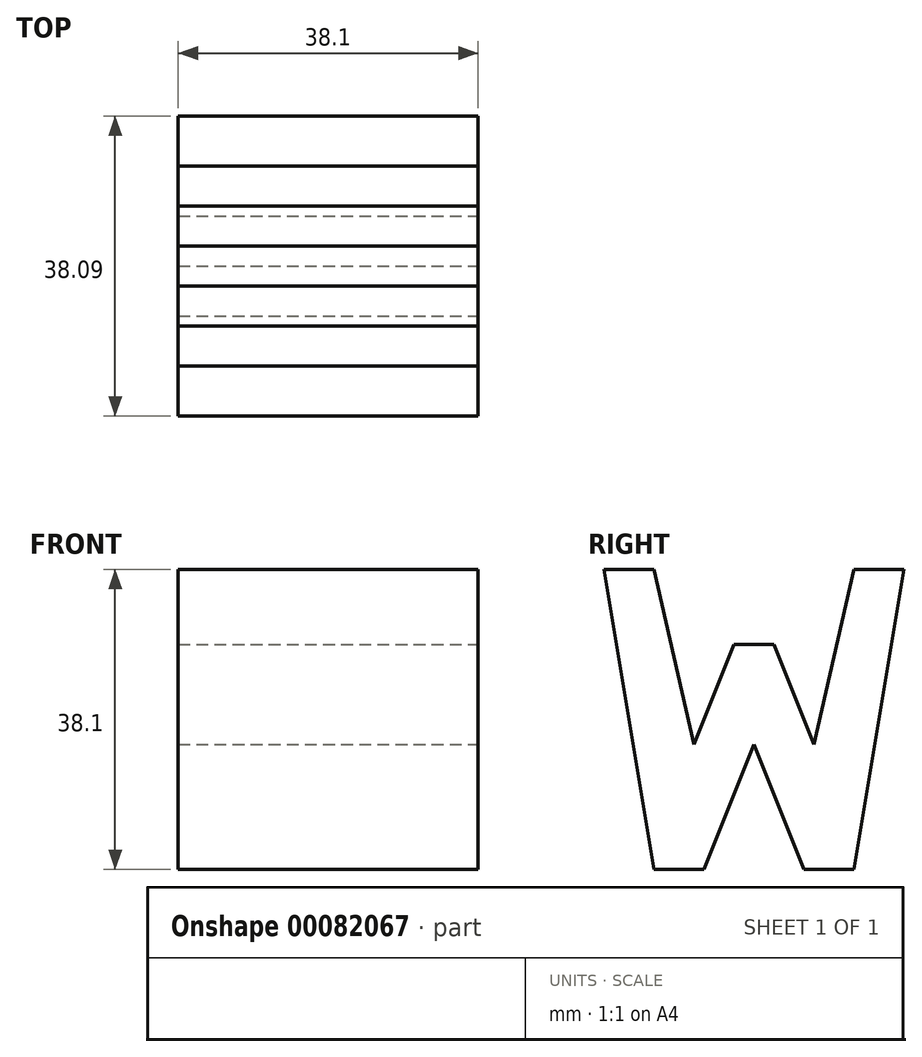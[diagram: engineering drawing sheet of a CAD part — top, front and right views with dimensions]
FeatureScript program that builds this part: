
annotation { "Feature Type Name" : "Feature", "Feature Type Description" : "" }
export const myFeature = defineFeature(function(context is Context, id is Id, definition is map)
    precondition{}
    {
        {
            var Q0;
            Q0=qCreatedBy(makeId("Front.planeOp"),FACE);
            var sketch = newSketch(context, id + "F0", { "sketchPlane" : qUnion([Q0])});
            skLineSegment(sketch, "E0", {"start": v(0, 0) * mm, "end": v(38.1, 0) * mm});
            skLineSegment(sketch, "E1", {"start": v(38.1, 0) * mm, "end": v(38.1, 38.1) * mm});
            skLineSegment(sketch, "E2", {"start": v(38.1, 38.1) * mm, "end": v(0, 38.1) * mm});
            skLineSegment(sketch, "E3", {"start": v(0, 38.1) * mm, "end": v(0, 0) * mm});
            skSolve(sketch);
        }
        {
            var Q0;
            Q0 = qSketchRegion(id + "F0", true);
            extrude(context, id + "F1", {"entities" : qUnion([Q0]), "depth" : 38.1 * mm});
        }
        {
            var Q0;
            Q0=qCreatedBy(makeId("Right.planeOp"),FACE);
            cPlane(context, id + "F2", {"entities" : qUnion([Q0]), "cplaneType" : CPlaneType.OFFSET, "offset" : 38.1 * mm, "width" : 152.4 * mm, "height" : 152.4 * mm});
        }
        {
            var Q0;
            Q0=qCreatedBy(id+"F2.planeOp",FACE);
            var sketch = newSketch(context, id + "F3", { "sketchPlane" : qUnion([Q0])});
            skLineSegment(sketch, "E4", {"start": v(-38.1, 38.14) * mm, "end": v(-31.75, 0) * mm});
            skLineSegment(sketch, "E5", {"start": v(-31.75, 0) * mm, "end": v(-25.4, 0) * mm});
            skLineSegment(sketch, "E6", {"start": v(-25.4, 0) * mm, "end": v(-19.05, 15.87) * mm});
            skLineSegment(sketch, "E7", {"start": v(-19.05, 15.88) * mm, "end": v(-12.7, 0) * mm});
            skLineSegment(sketch, "E8", {"start": v(-12.7, 0) * mm, "end": v(-6.35, 0) * mm});
            skLineSegment(sketch, "E9", {"start": v(-6.35, 0) * mm, "end": v(0, 38.1) * mm});
            skLineSegment(sketch, "E10", {"start": v(0, 38.1) * mm, "end": v(-6.35, 38.1) * mm});
            skLineSegment(sketch, "E11", {"start": v(-6.35, 38.1) * mm, "end": v(-11.43, 15.88) * mm});
            skLineSegment(sketch, "E12", {"start": v(-11.43, 15.88) * mm, "end": v(-16.51, 28.58) * mm});
            skLineSegment(sketch, "E13", {"start": v(-16.51, 28.58) * mm, "end": v(-21.6, 28.58) * mm});
            skLineSegment(sketch, "E14", {"start": v(-21.6, 28.58) * mm, "end": v(-26.67, 15.88) * mm});
            skLineSegment(sketch, "E15", {"start": v(-26.67, 15.88) * mm, "end": v(-31.75, 38.1) * mm});
            skLineSegment(sketch, "E16", {"start": v(-31.75, 38.1) * mm, "end": v(-38.1, 38.14) * mm});
            skLineSegment(sketch, "E17.bottom", {"start": v(0, 0) * mm, "end": v(-38.1, 0) * mm});
            skLineSegment(sketch, "E17.top", {"start": v(0, 38.14) * mm, "end": v(-38.1, 38.14) * mm});
            skLineSegment(sketch, "E17.left", {"start": v(0, 0) * mm, "end": v(0, 38.14) * mm});
            skLineSegment(sketch, "E17.right", {"start": v(-38.1, 0) * mm, "end": v(-38.1, 38.14) * mm});
            skSolve(sketch);
        }
        {
            var Q0;
            {var subQ0=sQuery(id+"F3.wireOp",EDGE,"E4");Q0=makeQuery(id+"F3.imprint","IMPRINT",FACE,{"disambiguationData":[TD([[makeQuery(id+"F3.imprint","IMPRINT",EDGE,{"derivedFrom":subQ0}),-1.0]])]});}
            var Q1;
            {var subQ0=sQuery(id+"F3.wireOp",EDGE,"E6");Q1=makeQuery(id+"F3.imprint","IMPRINT",FACE,{"disambiguationData":[TD([[makeQuery(id+"F3.imprint","IMPRINT",EDGE,{"derivedFrom":subQ0}),-1.0]])]});}
            var Q2;
            {var subQ0=sQuery(id+"F3.wireOp",EDGE,"E9");Q2=makeQuery(id+"F3.imprint","IMPRINT",FACE,{"disambiguationData":[TD([[makeQuery(id+"F3.imprint","IMPRINT",EDGE,{"derivedFrom":subQ0}),-1.0]])]});}
            var Q3;
            {var subQ0=sQuery(id+"F3.wireOp",EDGE,"E10");Q3=makeQuery(id+"F3.imprint","IMPRINT",FACE,{"disambiguationData":[TD([[makeQuery(id+"F3.imprint","IMPRINT",EDGE,{"derivedFrom":subQ0}),-1.0]])]});}
            extrude(context, id + "F4", {"entities" : qUnion([Q0, Q1, Q2, Q3]), "operationType" : NewBodyOperationType.REMOVE, "oppositeDirection" : true, "depth" : 38.1 * mm});
        }
    });
